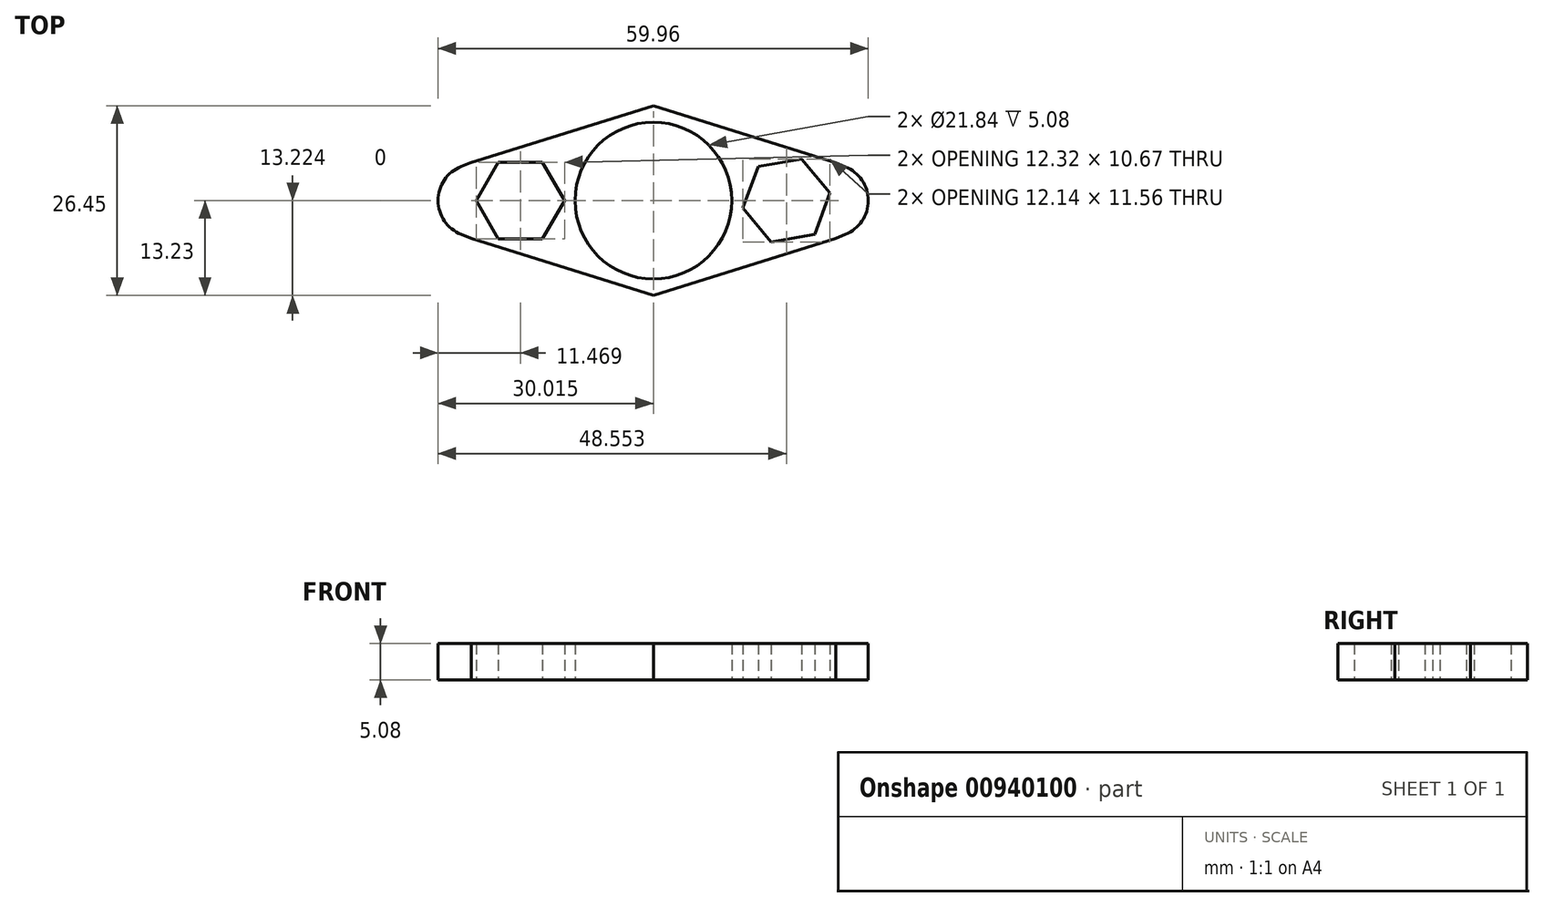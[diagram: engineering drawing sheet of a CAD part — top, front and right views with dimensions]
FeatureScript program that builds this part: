
annotation { "Feature Type Name" : "Feature", "Feature Type Description" : "" }
export const myFeature = defineFeature(function(context is Context, id is Id, definition is map)
    precondition{}
    {
        {
            var Q0;
            Q0=qCreatedBy(makeId("Top.planeOp"),FACE);
            var sketch = newSketch(context, id + "F0", { "sketchPlane" : qUnion([Q0])});
            skCircle(sketch, "E0", {"center": v(7.07, 0) * mm, "radius": 10.92 * mm});
            skLineSegment(sketch, "E1", {"start": v(32.46, 0) * mm, "end": v(31.03, 0) * mm});
            skLineSegment(sketch, "E2", {"start": v(7.07, 13.22) * mm, "end": v(-18.68, 13.22) * mm});
            skLineSegment(sketch, "E3", {"start": v(-18.68, 13.22) * mm, "end": v(-18.34, 0) * mm});
            skLineSegment(sketch, "E4", {"start": v(7.07, -13.23) * mm, "end": v(-18.34, -13.23) * mm});
            skLineSegment(sketch, "E5", {"start": v(-18.34, -13.23) * mm, "end": v(-18.34, 0) * mm});
            skLineSegment(sketch, "E6", {"start": v(7.07, -13.23) * mm, "end": v(32.46, -13.23) * mm});
            skLineSegment(sketch, "E7", {"start": v(32.46, -13.23) * mm, "end": v(32.46, 0) * mm});
            skLineSegment(sketch, "E8", {"start": v(32.46, 0) * mm, "end": v(32.46, 13.22) * mm});
            skLineSegment(sketch, "E9", {"start": v(32.46, 13.22) * mm, "end": v(7.07, 13.22) * mm});
            skLineSegment(sketch, "E10", {"start": v(32.46, 0) * mm, "end": v(25.6, 0) * mm});
            skLineSegment(sketch, "E11", {"start": v(-18.34, 0) * mm, "end": v(-11.48, 0) * mm});
            skCircle(sketch, "E12.cCircle", {"center": v(-11.48, 0) * mm, "radius": 5.33 * mm, "construction": true});
            skLineSegment(sketch, "E12.0", {"start": v(-8.4, -5.33) * mm, "end": v(-14.56, -5.33) * mm});
            skLineSegment(sketch, "E12.1", {"start": v(-14.56, -5.33) * mm, "end": v(-17.64, 0) * mm});
            skLineSegment(sketch, "E12.2", {"start": v(-17.64, 0) * mm, "end": v(-14.56, 5.33) * mm});
            skLineSegment(sketch, "E12.3", {"start": v(-14.56, 5.33) * mm, "end": v(-8.4, 5.33) * mm});
            skLineSegment(sketch, "E12.4", {"start": v(-8.4, 5.33) * mm, "end": v(-5.32, 0) * mm});
            skLineSegment(sketch, "E12.5", {"start": v(-5.32, 0) * mm, "end": v(-8.4, -5.33) * mm});
            skPoint(sketch, "E12.0.midPoint", {"position": v(-11.48, -5.33) * mm});
            skCircle(sketch, "E13.cCircle", {"center": v(25.6, 0) * mm, "radius": 5.33 * mm, "construction": true});
            skLineSegment(sketch, "E13.0", {"start": v(29.55, -4.73) * mm, "end": v(23.48, -5.78) * mm});
            skLineSegment(sketch, "E13.1", {"start": v(23.48, -5.78) * mm, "end": v(19.53, -1.05) * mm});
            skLineSegment(sketch, "E13.2", {"start": v(19.53, -1.05) * mm, "end": v(21.66, 4.73) * mm});
            skLineSegment(sketch, "E13.3", {"start": v(21.66, 4.73) * mm, "end": v(27.73, 5.78) * mm});
            skLineSegment(sketch, "E13.4", {"start": v(27.73, 5.78) * mm, "end": v(31.67, 1.05) * mm});
            skLineSegment(sketch, "E13.5", {"start": v(31.67, 1.05) * mm, "end": v(29.55, -4.73) * mm});
            skPoint(sketch, "E13.0.midPoint", {"position": v(26.51, -5.26) * mm});
            skLineSegment(sketch, "E14", {"start": v(7.07, -13.23) * mm, "end": v(-18.34, -5.25) * mm});
            skLineSegment(sketch, "E15", {"start": v(-18.34, -5.25) * mm, "end": v(-18.34, -13.23) * mm});
            skLineSegment(sketch, "E16", {"start": v(-18.68, 13.22) * mm, "end": v(-18.47, 5.25) * mm});
            skLineSegment(sketch, "E17", {"start": v(-18.47, 5.25) * mm, "end": v(7.07, 13.22) * mm});
            skLineSegment(sketch, "E18", {"start": v(32.46, 13.22) * mm, "end": v(32.46, 5.25) * mm});
            skLineSegment(sketch, "E19", {"start": v(32.46, 5.25) * mm, "end": v(7.07, 13.22) * mm});
            skLineSegment(sketch, "E20", {"start": v(32.46, -13.23) * mm, "end": v(32.46, -5.25) * mm});
            skLineSegment(sketch, "E21", {"start": v(32.46, -5.25) * mm, "end": v(7.07, -13.23) * mm});
            skLineSegment(sketch, "E22", {"start": v(-18.47, 5.25) * mm, "end": v(-31.65, 0) * mm});
            skLineSegment(sketch, "E23", {"start": v(-31.65, 0) * mm, "end": v(-18.34, -5.25) * mm});
            skLineSegment(sketch, "E24", {"start": v(-18.34, 0) * mm, "end": v(-31.65, 0) * mm});
            skLineSegment(sketch, "E25", {"start": v(32.46, 0) * mm, "end": v(45.77, 0) * mm});
            skLineSegment(sketch, "E26", {"start": v(45.77, 0) * mm, "end": v(32.46, 5.25) * mm});
            skLineSegment(sketch, "E27", {"start": v(45.77, 0) * mm, "end": v(32.46, -5.25) * mm});
            skSolve(sketch);
        }
        {
            var Q0;
            Q0=makeQuery(id+"F0.imprint","IMPRINT",FACE,{"disambiguationData":[TD([[makeQuery(id+"F0.imprint","IMPRINT",EDGE,{"derivedFrom":sQuery(id+"F0.wireOp",EDGE,"E3")}),-1.0]])]});
            var Q1;
            Q1=makeQuery(id+"F0.imprint","IMPRINT",FACE,{"disambiguationData":[TD([[makeQuery(id+"F0.imprint","IMPRINT",EDGE,{"derivedFrom":sQuery(id+"F0.wireOp",EDGE,"E5")}),1.0]])]});
            var Q2;
            Q2=makeQuery(id+"F0.imprint","IMPRINT",FACE,{"disambiguationData":[TD([[makeQuery(id+"F0.imprint","IMPRINT",EDGE,{"derivedFrom":sQuery(id+"F0.wireOp",EDGE,"E7")}),-1.0]])]});
            var Q3;
            Q3=makeQuery(id+"F0.imprint","IMPRINT",FACE,{"disambiguationData":[TD([[makeQuery(id+"F0.imprint","IMPRINT",EDGE,{"derivedFrom":sQuery(id+"F0.wireOp",EDGE,"E8")}),-1.0]])]});
            var Q4;
            Q4=makeQuery(id+"F0.imprint","IMPRINT",FACE,{"disambiguationData":[TD([[makeQuery(id+"F0.imprint","IMPRINT",EDGE,{"derivedFrom":sQuery(id+"F0.wireOp",EDGE,"E0")}),-1.0]])]});
            extrude(context, id + "F1", {"entities" : qUnion([Q0, Q1, Q2, Q3, Q4]), "depth" : 5.08 * mm, "offsetDistance" : 25.4 * mm});
        }
        {
            var Q0;
            Q0=makeQuery(id+"F1.opExtrude","SWEPT_EDGE",EDGE,{"disambiguationData":[OSD([sQuery(id+"F0.wireOp",EDGE,"E22"),sQuery(id+"F0.wireOp",EDGE,"E23"),sQuery(id+"F0.wireOp",EDGE,"E24")])]});
            var Q1;
            Q1=makeQuery(id+"F1.opExtrude","SWEPT_EDGE",EDGE,{"disambiguationData":[OSD([sQuery(id+"F0.wireOp",EDGE,"E25"),sQuery(id+"F0.wireOp",EDGE,"E26"),sQuery(id+"F0.wireOp",EDGE,"E27")])]});
            fillet(context, id + "F2", {"entities" : qUnion([Q0, Q1]), "radius" : 5.08 * mm, "tangentPropagation" : true, "allowEdgeOverflow" : false});
        }
    });
